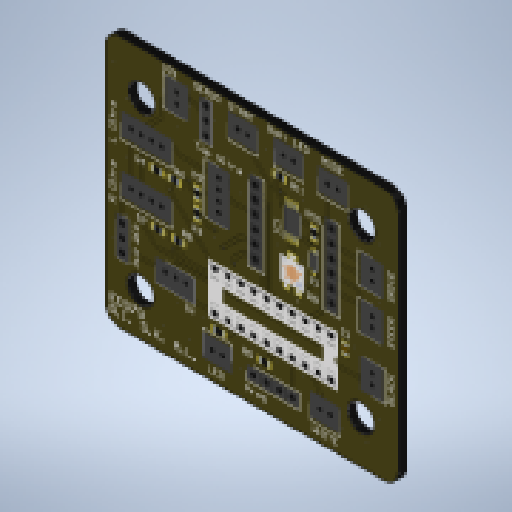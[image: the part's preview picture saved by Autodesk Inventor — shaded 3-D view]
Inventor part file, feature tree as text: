
AUTODESK INVENTOR PART (.ipt)
format: ipt  version: 2024.2 (Build 282272000, 272)  size: 487,936 bytes
history: native  units: in
note: dims shown in document units (in); Inventor stores cm internally (conversion verified against a paired STEP export)
features: other x4, sketch x2, imported_body x1
ambient origin geometry x8: Origin, YZ Plane, XZ Plane, XY Plane, X Axis, Y Axis, Z Axis, Center Point
bodies: Solid1 (feature_tree)
feature tree (7):
  other  "Decal1"
  other  "Decal2"
  sketch  "Sketch1"  dims[d12=0.0039in]
  other  "Image1"
  sketch  "Sketch2"  dims[d19=0.0059in d24=0.0118in d45=0.0in d46=0.0in d53=0.0in]
  other  "Image4"
  imported_body  "Base1"
